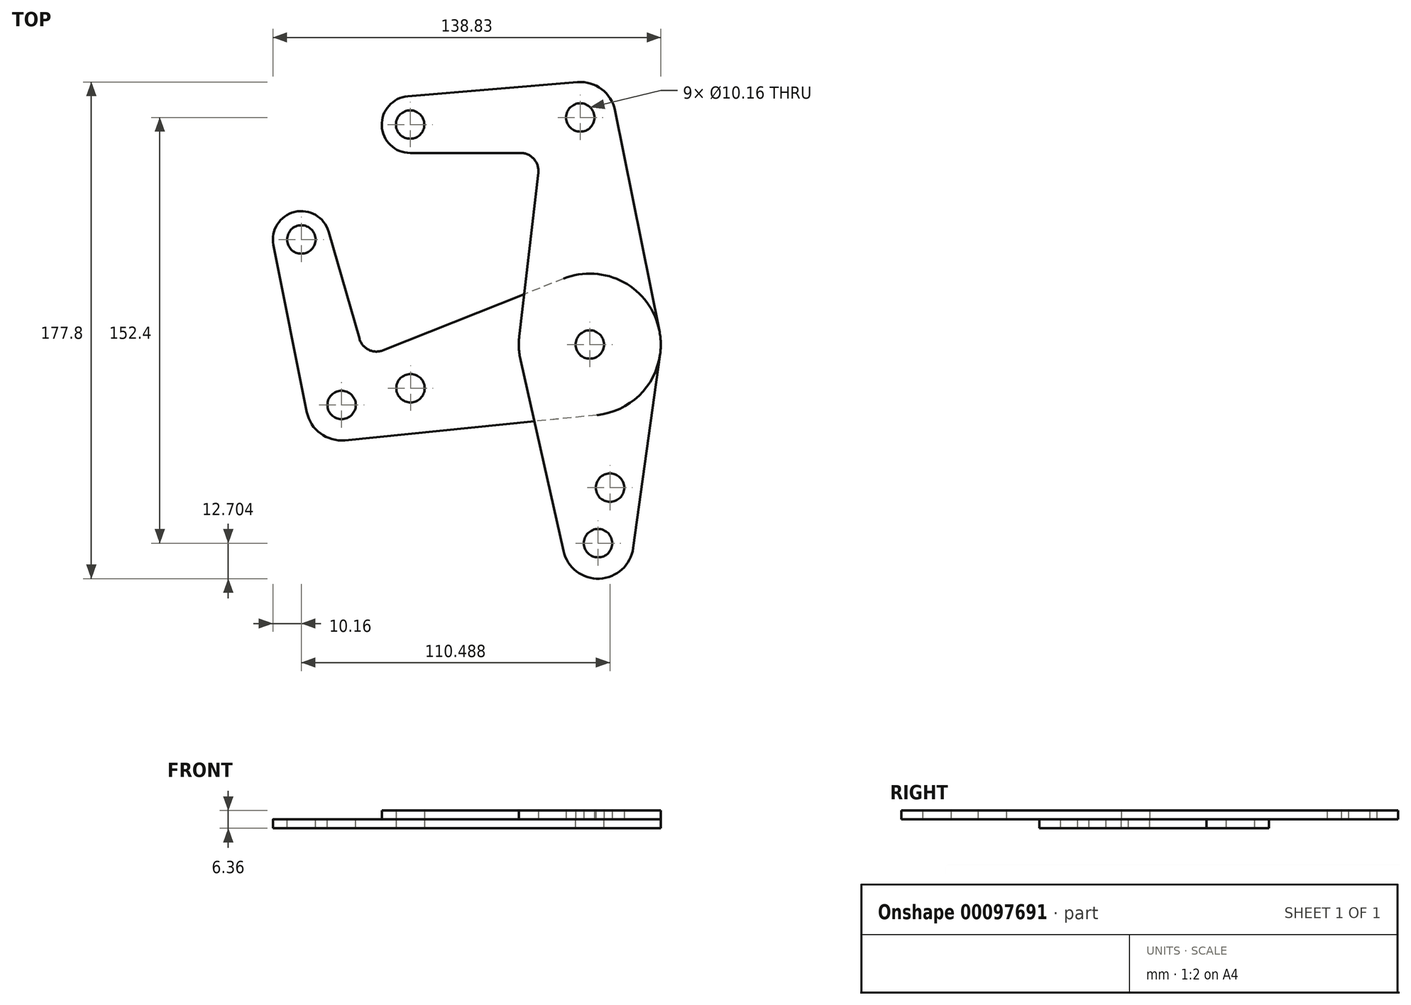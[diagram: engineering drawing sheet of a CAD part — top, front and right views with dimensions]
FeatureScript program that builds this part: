
annotation { "Feature Type Name" : "Feature", "Feature Type Description" : "" }
export const myFeature = defineFeature(function(context is Context, id is Id, definition is map)
    precondition{}
    {
        {
            var Q0;
            Q0=qCreatedBy(makeId("Top.planeOp"),FACE);
            var sketch = newSketch(context, id + "F0", { "sketchPlane" : qUnion([Q0])});
            skCircle(sketch, "E0", {"center": v(60.9, 102.91) * mm, "radius": 12.7 * mm});
            skCircle(sketch, "E1", {"center": v(60.9, 102.91) * mm, "radius": 5.08 * mm});
            skCircle(sketch, "E2", {"center": v(0, 100.37) * mm, "radius": 10.16 * mm});
            skCircle(sketch, "E3", {"center": v(0, 100.37) * mm, "radius": 5.08 * mm});
            skCircle(sketch, "E4", {"center": v(64.3, 21.63) * mm, "radius": 5.08 * mm});
            skCircle(sketch, "E5", {"center": v(64.3, 21.63) * mm, "radius": 25.4 * mm});
            skLineSegment(sketch, "E6", {"start": v(73.36, 105.42) * mm, "end": v(89.2, 26.64) * mm});
            skLineSegment(sketch, "E7", {"start": v(59.85, 115.57) * mm, "end": v(-0.85, 110.5) * mm});
            skCircle(sketch, "E8", {"center": v(-38.97, 59.23) * mm, "radius": 10.16 * mm});
            skCircle(sketch, "E9", {"center": v(-38.97, 59.23) * mm, "radius": 5.08 * mm});
            skCircle(sketch, "E10", {"center": v(-24.55, 0) * mm, "radius": 12.7 * mm});
            skCircle(sketch, "E11", {"center": v(-24.55, 0) * mm, "radius": 5.08 * mm});
            skCircle(sketch, "E12", {"center": v(67.26, -49.49) * mm, "radius": 12.7 * mm});
            skCircle(sketch, "E13", {"center": v(67.26, -49.49) * mm, "radius": 5.08 * mm});
            skLineSegment(sketch, "E14", {"start": v(60.9, 102.91) * mm, "end": v(0, 100.37) * mm, "construction": true});
            skLineSegment(sketch, "E15", {"start": v(89.46, 18.15) * mm, "end": v(79.84, -51.23) * mm});
            skLineSegment(sketch, "E16", {"start": v(39.51, 16.06) * mm, "end": v(54.87, -52.27) * mm});
            skLineSegment(sketch, "E17", {"start": v(-48.93, 57.24) * mm, "end": v(-37, -2.49) * mm});
            skLineSegment(sketch, "E18", {"start": v(66.82, -3.64) * mm, "end": v(-23.29, -12.64) * mm});
            skLineSegment(sketch, "E19", {"start": v(-38.97, 59.23) * mm, "end": v(-24.55, 0) * mm, "construction": true});
            skLineSegment(sketch, "E20", {"start": v(64.3, 21.63) * mm, "end": v(-24.55, 0) * mm, "construction": true});
            skCircle(sketch, "E21", {"center": v(71.52, -29.62) * mm, "radius": 5.08 * mm});
            skCircle(sketch, "E22", {"center": v(0.13, 6) * mm, "radius": 5.08 * mm});
            skLineSegment(sketch, "E23", {"start": v(39.06, 24.55) * mm, "end": v(45.84, 83.14) * mm});
            skLineSegment(sketch, "E24", {"start": v(0, 90.21) * mm, "end": v(39.53, 90.21) * mm});
            skLineSegment(sketch, "E25", {"start": v(-29.2, 62.04) * mm, "end": v(-18.16, 23.7) * mm});
            skLineSegment(sketch, "E26", {"start": v(54.92, 45.24) * mm, "end": v(-9.71, 19.56) * mm});
            skLineSegment(sketch, "E27", {"start": v(60.9, 102.91) * mm, "end": v(64.3, 21.63) * mm, "construction": true});
            skLineSegment(sketch, "E28", {"start": v(64.3, 21.63) * mm, "end": v(67.26, -49.49) * mm, "construction": true});
            skArc(sketch, "E29.filletArc", {"start": v(45.84, 83.14) * mm, "mid": v(44.27, 88.09) * mm, "end": v(39.53, 90.21) * mm});
            skArc(sketch, "E30.filletArc", {"start": v(-18.16, 23.7) * mm, "mid": v(-14.85, 19.76) * mm, "end": v(-9.71, 19.56) * mm});
            skSolve(sketch);
        }
        {
            var Q0;
            Q0=makeQuery(id+"F0.imprint","IMPRINT",FACE,{"disambiguationData":[TD([[makeQuery(id+"F0.imprint","IMPRINT",EDGE,{"derivedFrom":sQuery(id+"F0.wireOp",EDGE,"E3")}),-1.0]])]});
            var Q1;
            Q1=makeQuery(id+"F0.imprint","IMPRINT",FACE,{"disambiguationData":[TD([[makeQuery(id+"F0.imprint","IMPRINT",EDGE,{"derivedFrom":sQuery(id+"F0.wireOp",EDGE,"E13")}),-1.0]])]});
            var Q2;
            {var subQ5=sQuery(id+"F0.wireOp",EDGE,"E7");Q2=makeQuery(id+"F0.imprint","IMPRINT",FACE,{"disambiguationData":[TD([[makeQuery(id+"F0.imprint","IMPRINT",EDGE,{"derivedFrom":subQ5}),1.0]])]});}
            var Q3;
            {var subQ0=sQuery(id+"F0.wireOp",EDGE,"E23");var subQ1=sQuery(id+"F0.wireOp",EDGE,"E0");var subQ2=makeQuery(id+"F0.imprint","INTERSECT",VERTEX,{"derivedFrom":[subQ1,subQ0]});Q3=makeQuery(id+"F0.imprint","IMPRINT",FACE,{"disambiguationData":[TD([[makeQuery(id+"F0.imprint","IMPRINT",EDGE,{"disambiguationData":[TD([[subQ2,-1.0]])],"derivedFrom":subQ1}),-1.0]])]});}
            var Q4;
            {var subQ0=sQuery(id+"F0.wireOp",EDGE,"E23");var subQ1=sQuery(id+"F0.wireOp",EDGE,"E5");var subQ2=makeQuery(id+"F0.imprint","INTERSECT",VERTEX,{"derivedFrom":[subQ1,subQ0]});Q4=makeQuery(id+"F0.imprint","IMPRINT",FACE,{"disambiguationData":[TD([[makeQuery(id+"F0.imprint","IMPRINT",EDGE,{"disambiguationData":[TD([[subQ2,1.0]])],"derivedFrom":subQ1}),-1.0]])]});}
            var Q5;
            {var subQ0=sQuery(id+"F0.wireOp",EDGE,"E16");var subQ1=sQuery(id+"F0.wireOp",EDGE,"E5");var subQ2=makeQuery(id+"F0.imprint","INTERSECT",VERTEX,{"derivedFrom":[subQ1,subQ0]});Q5=makeQuery(id+"F0.imprint","IMPRINT",FACE,{"disambiguationData":[TD([[makeQuery(id+"F0.imprint","IMPRINT",EDGE,{"disambiguationData":[TD([[subQ2,-1.0]])],"derivedFrom":subQ1}),-1.0]])]});}
            var Q6;
            Q6=makeQuery(id+"F0.imprint","IMPRINT",FACE,{"disambiguationData":[TD([[makeQuery(id+"F0.imprint","IMPRINT",EDGE,{"derivedFrom":sQuery(id+"F0.wireOp",EDGE,"E1")}),-1.0]])]});
            var Q7;
            {var subQ5=sQuery(id+"F0.wireOp",EDGE,"E6");Q7=makeQuery(id+"F0.imprint","IMPRINT",FACE,{"disambiguationData":[TD([[makeQuery(id+"F0.imprint","IMPRINT",EDGE,{"derivedFrom":subQ5}),-1.0]])]});}
            var Q8;
            {var subQ0=sQuery(id+"F0.wireOp",EDGE,"E15");Q8=makeQuery(id+"F0.imprint","IMPRINT",FACE,{"disambiguationData":[TD([[makeQuery(id+"F0.imprint","IMPRINT",EDGE,{"derivedFrom":subQ0}),-1.0]])]});}
            var Q9;
            Q9=makeQuery(id+"F0.imprint","IMPRINT",FACE,{"disambiguationData":[TD([[makeQuery(id+"F0.imprint","IMPRINT",EDGE,{"derivedFrom":sQuery(id+"F0.wireOp",EDGE,"E4")}),-1.0]])]});
            extrude(context, id + "F1", {"entities" : qUnion([Q0, Q1, Q2, Q3, Q4, Q5, Q6, Q7, Q8, Q9]), "depth" : 3.17 * mm});
        }
        {
            var Q0;
            Q0=makeQuery(id+"F0.imprint","IMPRINT",FACE,{"disambiguationData":[TD([[makeQuery(id+"F0.imprint","IMPRINT",EDGE,{"derivedFrom":sQuery(id+"F0.wireOp",EDGE,"E9")}),-1.0]])]});
            var Q1;
            Q1=makeQuery(id+"F0.imprint","IMPRINT",FACE,{"disambiguationData":[TD([[makeQuery(id+"F0.imprint","IMPRINT",EDGE,{"derivedFrom":sQuery(id+"F0.wireOp",EDGE,"E11")}),-1.0]])]});
            var Q2;
            {var subQ0=sQuery(id+"F0.wireOp",EDGE,"E23");var subQ1=sQuery(id+"F0.wireOp",EDGE,"E5");var subQ2=makeQuery(id+"F0.imprint","INTERSECT",VERTEX,{"derivedFrom":[subQ1,subQ0]});Q2=makeQuery(id+"F0.imprint","IMPRINT",FACE,{"disambiguationData":[TD([[makeQuery(id+"F0.imprint","IMPRINT",EDGE,{"disambiguationData":[TD([[subQ2,1.0]])],"derivedFrom":subQ1}),-1.0]])]});}
            var Q3;
            {var subQ0=sQuery(id+"F0.wireOp",EDGE,"E16");var subQ1=sQuery(id+"F0.wireOp",EDGE,"E5");var subQ2=makeQuery(id+"F0.imprint","INTERSECT",VERTEX,{"derivedFrom":[subQ1,subQ0]});Q3=makeQuery(id+"F0.imprint","IMPRINT",FACE,{"disambiguationData":[TD([[makeQuery(id+"F0.imprint","IMPRINT",EDGE,{"disambiguationData":[TD([[subQ2,-1.0]])],"derivedFrom":subQ1}),-1.0]])]});}
            var Q4;
            Q4=makeQuery(id+"F0.imprint","IMPRINT",FACE,{"disambiguationData":[TD([[makeQuery(id+"F0.imprint","IMPRINT",EDGE,{"derivedFrom":sQuery(id+"F0.wireOp",EDGE,"E4")}),-1.0]])]});
            var Q5;
            {var subQ13=sQuery(id+"F0.wireOp",EDGE,"E17");Q5=makeQuery(id+"F0.imprint","IMPRINT",FACE,{"disambiguationData":[TD([[makeQuery(id+"F0.imprint","IMPRINT",EDGE,{"derivedFrom":subQ13}),1.0]])]});}
            extrude(context, id + "F2", {"entities" : qUnion([Q0, Q1, Q2, Q3, Q4, Q5]), "oppositeDirection" : true, "depth" : 3.17 * mm});
        }
    });
